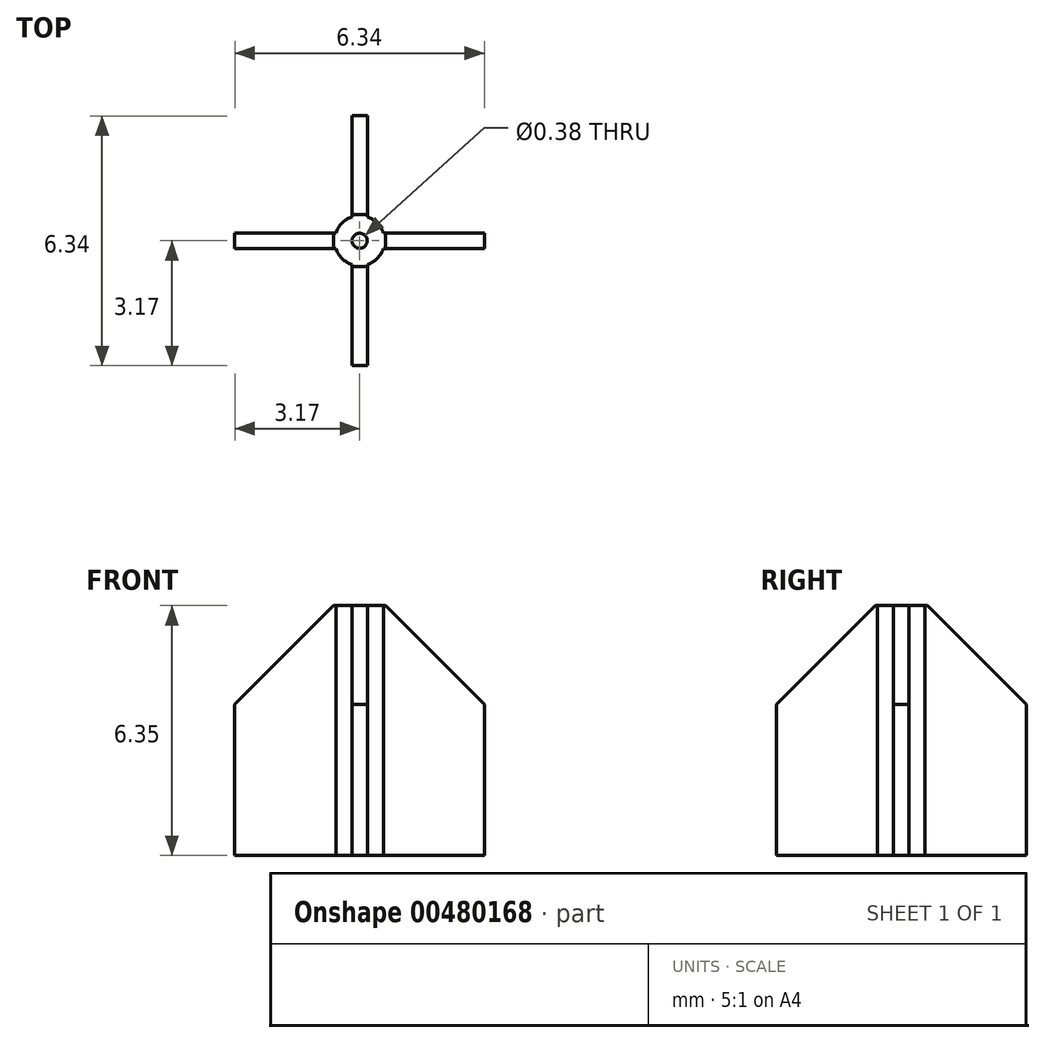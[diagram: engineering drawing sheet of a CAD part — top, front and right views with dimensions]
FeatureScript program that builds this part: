
annotation { "Feature Type Name" : "Feature", "Feature Type Description" : "" }
export const myFeature = defineFeature(function(context is Context, id is Id, definition is map)
    precondition{}
    {
        {
            var Q0;
            Q0=qCreatedBy(makeId("Top.planeOp"),FACE);
            var sketch = newSketch(context, id + "F0", { "sketchPlane" : qUnion([Q0])});
            skLineSegment(sketch, "E0.bottom", {"start": v(3.18, -0.2) * mm, "end": v(0.6, -0.2) * mm});
            skLineSegment(sketch, "E0.top", {"start": v(3.18, 0.2) * mm, "end": v(0.6, 0.2) * mm});
            skLineSegment(sketch, "E0.left", {"start": v(3.18, -0.2) * mm, "end": v(3.18, 0.2) * mm});
            skLineSegment(sketch, "E0.right", {"start": v(-3.18, -0.2) * mm, "end": v(-3.18, 0.2) * mm});
            skPoint(sketch, "E0.middle", {"position": v(0, 0) * mm});
            skLineSegment(sketch, "E1.bottom", {"start": v(-0.2, 3.17) * mm, "end": v(0.2, 3.17) * mm});
            skLineSegment(sketch, "E1.top", {"start": v(-0.2, -3.18) * mm, "end": v(0.2, -3.18) * mm});
            skLineSegment(sketch, "E1.left", {"start": v(-0.2, 3.17) * mm, "end": v(-0.2, 0.6) * mm});
            skLineSegment(sketch, "E1.right", {"start": v(0.2, 3.17) * mm, "end": v(0.2, 0.6) * mm});
            skLineSegment(sketch, "E2.trimOffspring", {"start": v(-0.6, 0.2) * mm, "end": v(-3.18, 0.2) * mm});
            skLineSegment(sketch, "E3.trimOffspring", {"start": v(-0.6, -0.2) * mm, "end": v(-3.18, -0.2) * mm});
            skLineSegment(sketch, "E4.trimOffspring", {"start": v(-0.2, -0.6) * mm, "end": v(-0.2, -3.18) * mm});
            skLineSegment(sketch, "E5.trimOffspring", {"start": v(0.2, -0.6) * mm, "end": v(0.2, -3.18) * mm});
            skArc(sketch, "E6", {"start": v(-0.6, -0.2) * mm, "mid": v(-0.45, -0.45) * mm, "end": v(-0.2, -0.6) * mm});
            skArc(sketch, "E7.trimOffspring", {"start": v(0.2, -0.6) * mm, "mid": v(0.45, -0.45) * mm, "end": v(0.6, -0.2) * mm});
            skArc(sketch, "E8.trimOffspring", {"start": v(0.6, 0.2) * mm, "mid": v(0.45, 0.45) * mm, "end": v(0.2, 0.6) * mm});
            skArc(sketch, "E9.trimOffspring", {"start": v(-0.2, 0.6) * mm, "mid": v(-0.45, 0.45) * mm, "end": v(-0.6, 0.2) * mm});
            skCircle(sketch, "E10", {"center": v(0, 0) * mm, "radius": 0.2 * mm});
            skSolve(sketch);
        }
        {
            var Q0;
            Q0=makeQuery(id+"F0.imprint","IMPRINT",FACE,{"disambiguationData":[TD([[makeQuery(id+"F0.imprint","IMPRINT",EDGE,{"derivedFrom":sQuery(id+"F0.wireOp",EDGE,"E0.bottom")}),-1.0]])]});
            extrude(context, id + "F1", {"entities" : qUnion([Q0]), "depth" : 6.35 * mm});
        }
        {
            var Q0;
            Q0=makeQuery(id+"F1.opExtrude","CAP_EDGE",EDGE,{"disambiguationData":[OSD([sQuery(id+"F0.wireOp",EDGE,"E1.top")])],"isStart":false});
            var Q1;
            Q1=makeQuery(id+"F1.opExtrude","CAP_EDGE",EDGE,{"disambiguationData":[OSD([sQuery(id+"F0.wireOp",EDGE,"E0.right")])],"isStart":false});
            var Q2;
            Q2=makeQuery(id+"F1.opExtrude","CAP_EDGE",EDGE,{"disambiguationData":[OSD([sQuery(id+"F0.wireOp",EDGE,"E0.left")])],"isStart":false});
            var Q3;
            Q3=makeQuery(id+"F1.opExtrude","CAP_EDGE",EDGE,{"disambiguationData":[OSD([sQuery(id+"F0.wireOp",EDGE,"E1.bottom")])],"isStart":false});
            chamfer(context, id + "F2", {"entities" : qUnion([Q0, Q1, Q2, Q3]), "width" : 2.5 * mm, "tangentPropagation" : true});
        }
    });
